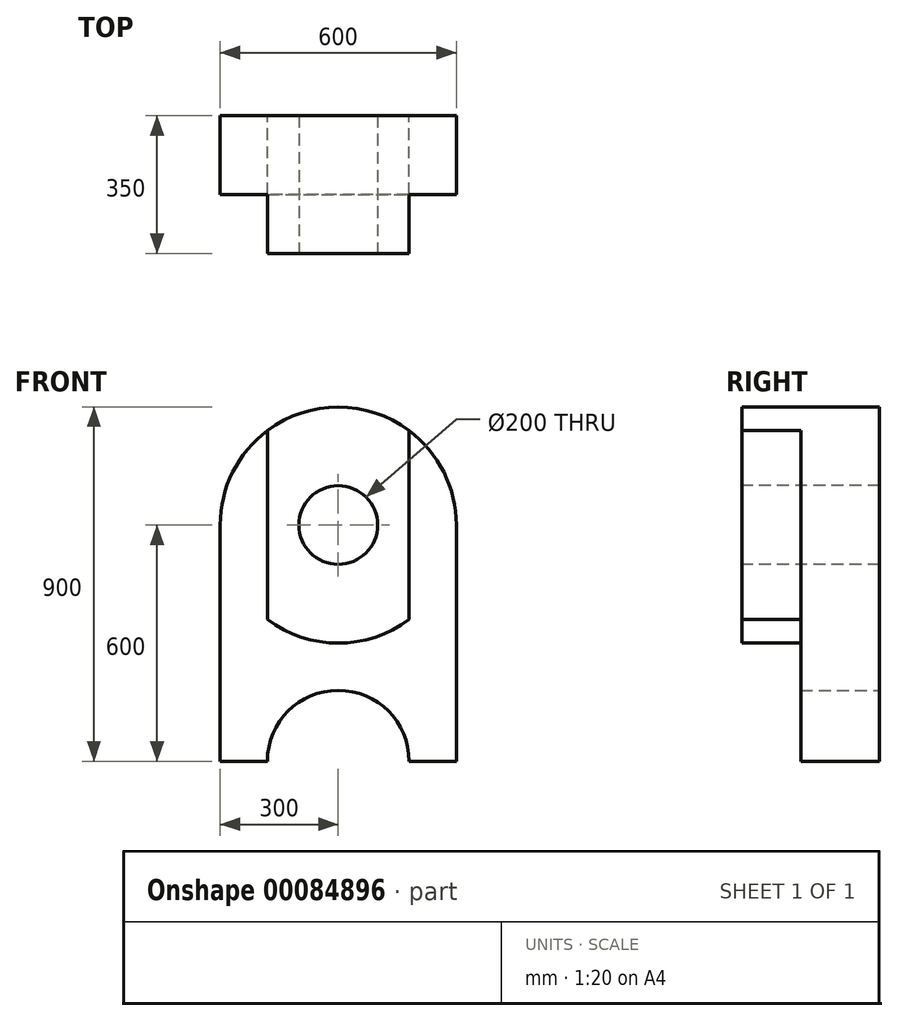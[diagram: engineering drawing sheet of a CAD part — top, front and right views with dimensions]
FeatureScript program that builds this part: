
annotation { "Feature Type Name" : "Feature", "Feature Type Description" : "" }
export const myFeature = defineFeature(function(context is Context, id is Id, definition is map)
    precondition{}
    {
        {
            var Q0;
            Q0=qCreatedBy(makeId("Front.planeOp"),FACE);
            var sketch = newSketch(context, id + "F0", { "sketchPlane" : qUnion([Q0])});
            skLineSegment(sketch, "E0.bottom", {"start": v(-300, -300) * mm, "end": v(-180, -300) * mm});
            skLineSegment(sketch, "E0.left", {"start": v(-300, -300) * mm, "end": v(-300, 300) * mm});
            skLineSegment(sketch, "E0.right", {"start": v(300, -300) * mm, "end": v(300, 300) * mm});
            skPoint(sketch, "E0.middle", {"position": v(0, 0) * mm});
            skArc(sketch, "E1", {"start": v(180, -300) * mm, "mid": v(0, -120) * mm, "end": v(-180, -300) * mm});
            skLineSegment(sketch, "E2.trimOffspring", {"start": v(180, -300) * mm, "end": v(300, -300) * mm});
            skArc(sketch, "E3", {"start": v(300, 300) * mm, "mid": v(0, 600) * mm, "end": v(-300, 300) * mm});
            skPoint(sketch, "E4.middle", {"position": v(0, 600) * mm});
            skArc(sketch, "E5", {"start": v(0, 0) * mm, "mid": v(0.02, 0) * mm, "end": v(0.03, 0) * mm});
            skPoint(sketch, "E6.orphan", {"position": v(179.97, 1140.02) * mm});
            skPoint(sketch, "E7.orphan", {"position": v(-180.03, 1139.98) * mm});
            skPoint(sketch, "E8.orphan", {"position": v(0.03, 0) * mm});
            skPoint(sketch, "E9.center.orphan", {"position": v(0, 325.92) * mm});
            skPoint(sketch, "E4.left.end.orphan", {"position": v(-180, 540) * mm});
            skPoint(sketch, "E4.right.end.orphan", {"position": v(180, 540) * mm});
            skPoint(sketch, "E10.orphan", {"position": v(180.03, 60.02) * mm});
            skPoint(sketch, "E11.orphan", {"position": v(-179.97, 59.98) * mm});
            skSolve(sketch);
        }
        {
            var Q0;
            Q0 = qSketchRegion(id + "F0", true);
            extrude(context, id + "F1", {"entities" : qUnion([Q0]), "depth" : 200 * mm});
        }
        {
            var Q0;
            Q0=makeQuery(id+"F1.opExtrude","CAP_FACE",FACE,{"disambiguationData":[OSD([sQuery(id+"F0.wireOp",EDGE,"E0.bottom"),sQuery(id+"F0.wireOp",EDGE,"E0.left"),sQuery(id+"F0.wireOp",EDGE,"E0.right"),sQuery(id+"F0.wireOp",EDGE,"E1"),sQuery(id+"F0.wireOp",EDGE,"E2.trimOffspring"),sQuery(id+"F0.wireOp",EDGE,"E3")])],"isStart":false});
            var sketch = newSketch(context, id + "F2", { "sketchPlane" : qUnion([Q0])});
            skLineSegment(sketch, "E12.left", {"start": v(-179.93, 59.95) * mm, "end": v(-180, 540) * mm});
            skLineSegment(sketch, "E12.right", {"start": v(180.07, 60.05) * mm, "end": v(180, 540) * mm});
            skPoint(sketch, "E12.middle", {"position": v(0, 600) * mm});
            skArc(sketch, "E13.trimOffspring", {"start": v(-179.93, 59.95) * mm, "mid": v(0.08, 0) * mm, "end": v(180.07, 60.05) * mm});
            skPoint(sketch, "E14.orphan", {"position": v(-180.07, 1139.95) * mm});
            skPoint(sketch, "E15.orphan", {"position": v(179.93, 1140.05) * mm});
            skArc(sketch, "E16", {"start": v(180, 540) * mm, "mid": v(0, 600) * mm, "end": v(-180, 540) * mm});
            skSolve(sketch);
        }
        {
            var Q0;
            Q0 = qSketchRegion(id + "F2", true);
            extrude(context, id + "F3", {"entities" : qUnion([Q0]), "operationType" : NewBodyOperationType.ADD, "depth" : 150 * mm});
        }
        {
            var Q0;
            Q0=makeQuery(id+"F3.opExtrude","CAP_FACE",FACE,{"disambiguationData":[OSD([sQuery(id+"F2.wireOp",EDGE,"E12.left"),sQuery(id+"F2.wireOp",EDGE,"E12.right"),sQuery(id+"F2.wireOp",EDGE,"E13.trimOffspring"),sQuery(id+"F2.wireOp",EDGE,"E16")])],"isStart":false});
            var sketch = newSketch(context, id + "F4", { "sketchPlane" : qUnion([Q0])});
            skCircle(sketch, "E17", {"center": v(0, 300) * mm, "radius": 100 * mm});
            skSolve(sketch);
        }
        {
            var Q0;
            Q0 = qSketchRegion(id + "F4", true);
            extrude(context, id + "F5", {"entities" : qUnion([Q0]), "operationType" : NewBodyOperationType.REMOVE, "endBound" : BoundingType.THROUGH_ALL, "oppositeDirection" : true, "depth" : 25 * mm});
        }
    });
